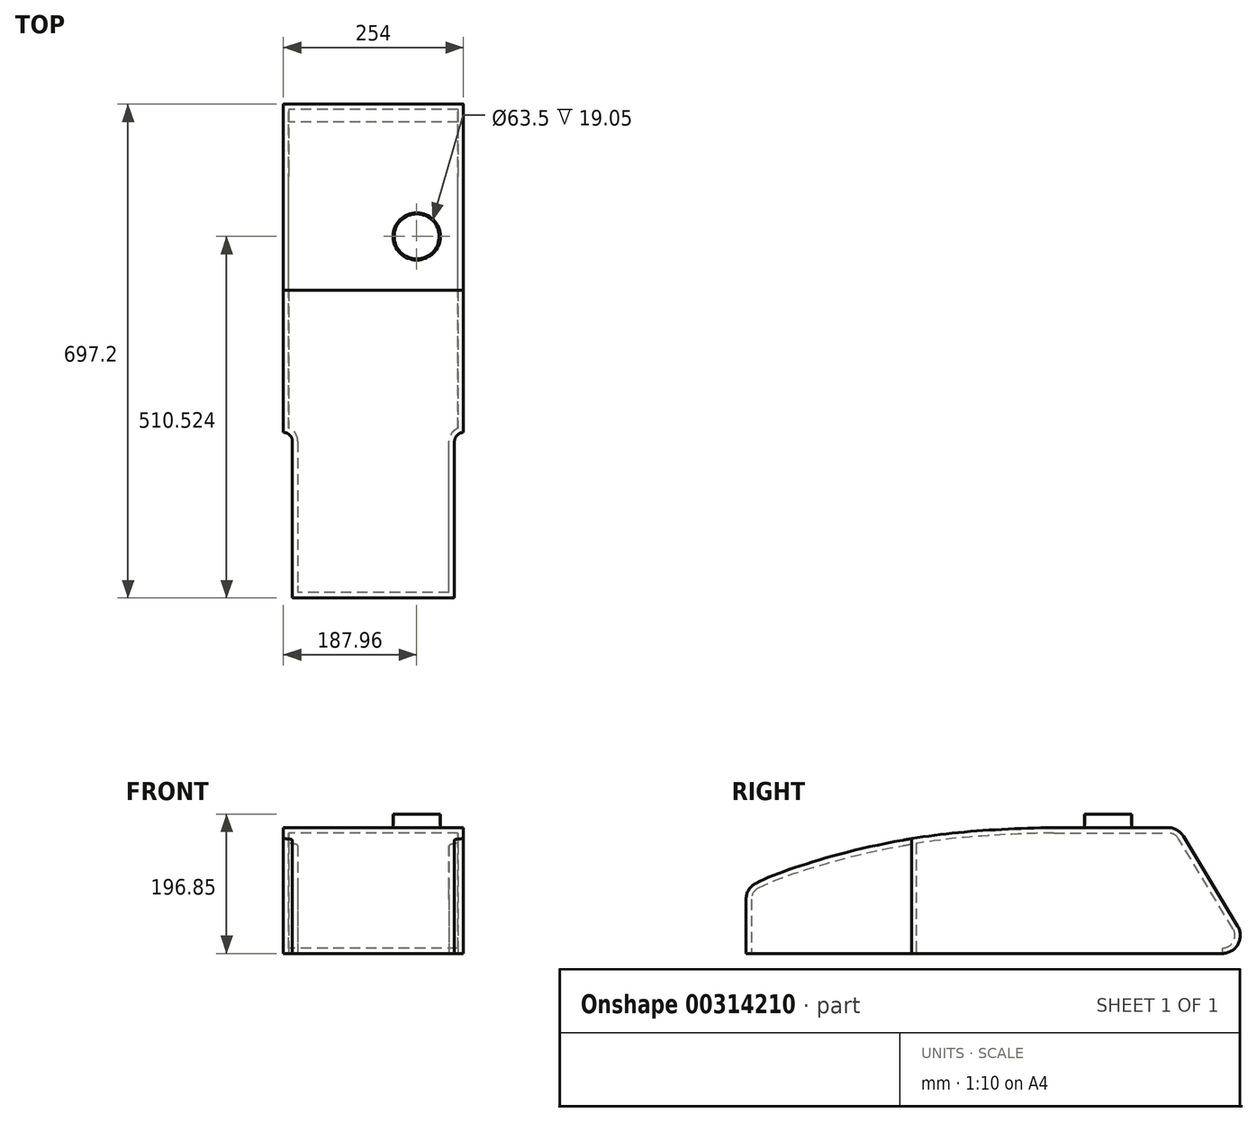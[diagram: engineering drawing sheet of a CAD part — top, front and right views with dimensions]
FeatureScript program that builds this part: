
annotation { "Feature Type Name" : "Feature", "Feature Type Description" : "" }
export const myFeature = defineFeature(function(context is Context, id is Id, definition is map)
    precondition{}
    {
        {
            var Q0;
            Q0=qCreatedBy(makeId("Right.planeOp"),FACE);
            var sketch = newSketch(context, id + "F0", { "sketchPlane" : qUnion([Q0])});
            skLineSegment(sketch, "E0", {"start": v(0, 0) * mm, "end": v(671.8, 0) * mm});
            skLineSegment(sketch, "E1", {"start": v(693.55, 38.52) * mm, "end": v(616.94, 165.52) * mm});
            skLineSegment(sketch, "E2", {"start": v(434.32, 177.8) * mm, "end": v(595.2, 177.8) * mm});
            skLineSegment(sketch, "E3", {"start": v(609.53, 177.8) * mm, "end": v(609.53, 0) * mm, "construction": true});
            skFitSpline(sketch, "E4", {"points": [v(609.53, 177.8) * mm, v(271.41, 167.5) * mm, v(75.93, 123.59) * mm, v(0, 91) * mm, v(-33.15, 62.68) * mm], "startDerivative": vector(-932.62, 8.95) * mm, "endDerivative": vector(-216.23, -214.76) * mm});
            skLineSegment(sketch, "E5", {"start": v(0, 76.41) * mm, "end": v(0, 0) * mm});
            skPoint(sketch, "E6.visualSharp", {"position": v(716.79, 0) * mm});
            skArc(sketch, "E6.filletArc", {"start": v(671.8, 0) * mm, "mid": v(693.92, 12.91) * mm, "end": v(693.55, 38.52) * mm});
            skPoint(sketch, "E7.newPointA", {"position": v(694.44, 177.8) * mm});
            skPoint(sketch, "E7.newPointB", {"position": v(585.59, 217.5) * mm});
            skArc(sketch, "E7.filletArc", {"start": v(616.94, 165.52) * mm, "mid": v(607.68, 174.52) * mm, "end": v(595.2, 177.8) * mm});
            skArc(sketch, "E8.filletArc", {"start": v(13.66, 98.93) * mm, "mid": v(3.68, 89.58) * mm, "end": v(0, 76.41) * mm});
            skPoint(sketch, "E9.orphan", {"position": v(-16.76, 177.8) * mm});
            skSolve(sketch);
        }
        {
            var Q0;
            Q0=makeQuery(id+"F0.imprint","IMPRINT",FACE,{"disambiguationData":[TD([[makeQuery(id+"F0.imprint","IMPRINT",EDGE,{"derivedFrom":sQuery(id+"F0.wireOp",EDGE,"E0")}),1.0]])]});
            extrude(context, id + "F1", {"entities" : qUnion([Q0]), "endBound" : BoundingType.SYMMETRIC, "depth" : 254 * mm});
        }
        {
            var Q0;
            Q0=qCreatedBy(makeId("Top.planeOp"),FACE);
            var sketch = newSketch(context, id + "F2", { "sketchPlane" : qUnion([Q0])});
            skLineSegment(sketch, "E10", {"start": v(0, 0) * mm, "end": v(0, 736.6) * mm, "construction": true});
            skLineSegment(sketch, "E11", {"start": v(0, 0) * mm, "end": v(-114.3, 0) * mm});
            skLineSegment(sketch, "E12", {"start": v(0, 0) * mm, "end": v(114.3, 0) * mm});
            skPoint(sketch, "E13", {"position": v(-114.3, 0) * mm});
            skPoint(sketch, "E14.visualSharp", {"position": v(-114.3, 233.68) * mm});
            skPoint(sketch, "E15.visualSharp", {"position": v(114.3, 233.68) * mm});
            skLineSegment(sketch, "E16", {"start": v(-114.3, 220.98) * mm, "end": v(-114.3, 0) * mm});
            skLineSegment(sketch, "E17", {"start": v(-127, 233.68) * mm, "end": v(-127, 233.68) * mm});
            skLineSegment(sketch, "E18", {"start": v(-114.3, 0) * mm, "end": v(-127, 0) * mm});
            skLineSegment(sketch, "E19", {"start": v(-127, 0) * mm, "end": v(-127, 233.68) * mm});
            skLineSegment(sketch, "E20", {"start": v(114.3, 0) * mm, "end": v(114.3, 220.98) * mm});
            skLineSegment(sketch, "E21", {"start": v(127, 233.68) * mm, "end": v(127, 0) * mm});
            skLineSegment(sketch, "E22", {"start": v(127, 0) * mm, "end": v(114.3, 0) * mm});
            skArc(sketch, "E23.filletArc", {"start": v(-114.3, 220.98) * mm, "mid": v(-118.02, 229.96) * mm, "end": v(-127, 233.68) * mm});
            skLineSegment(sketch, "E24", {"start": v(127, 233.68) * mm, "end": v(127, 233.68) * mm});
            skArc(sketch, "E25.filletArc", {"start": v(127, 233.68) * mm, "mid": v(118.02, 229.96) * mm, "end": v(114.3, 220.98) * mm});
            skSolve(sketch);
        }
        {
            var Q0;
            Q0=makeQuery(id+"F2.imprint","IMPRINT",FACE,{"disambiguationData":[TD([[makeQuery(id+"F2.imprint","IMPRINT",EDGE,{"derivedFrom":sQuery(id+"F2.wireOp",EDGE,"E16")}),-1.0]])]});
            var Q1;
            Q1=makeQuery(id+"F2.imprint","IMPRINT",FACE,{"disambiguationData":[TD([[makeQuery(id+"F2.imprint","IMPRINT",EDGE,{"derivedFrom":sQuery(id+"F2.wireOp",EDGE,"E20")}),-1.0]])]});
            extrude(context, id + "F3", {"entities" : qUnion([Q0, Q1]), "operationType" : NewBodyOperationType.REMOVE, "depth" : 177.8 * mm});
        }
        {
            var Q0;
            Q0=makeQuery(id+"F1.opExtrude","SWEPT_FACE",FACE,{"disambiguationData":[OSD([sQuery(id+"F0.wireOp",EDGE,"E2")])]});
            var sketch = newSketch(context, id + "F4", { "sketchPlane" : qUnion([Q0])});
            skCircle(sketch, "E26", {"center": v(60.96, 510.52) * mm, "radius": 31.75 * mm});
            skLineSegment(sketch, "E27", {"start": v(0, 434.32) * mm, "end": v(0, 638.93) * mm, "construction": true});
            skCircle(sketch, "E28.0", {"center": v(60.96, 510.52) * mm, "radius": 33.34 * mm});
            skSolve(sketch);
        }
        {
            var Q0;
            Q0=makeQuery(id+"F4.imprint","IMPRINT",FACE,{"disambiguationData":[TD([[makeQuery(id+"F4.imprint","IMPRINT",EDGE,{"derivedFrom":sQuery(id+"F4.wireOp",EDGE,"E26")}),-1.0]])]});
            extrude(context, id + "F5", {"entities" : qUnion([Q0]), "operationType" : NewBodyOperationType.ADD, "depth" : 19.05 * mm});
        }
        {
            var Q0;
            Q0=makeQuery(id+"F1.opExtrude","SWEPT_FACE",FACE,{"disambiguationData":[OSD([sQuery(id+"F0.wireOp",EDGE,"E0")])]});
            shell(context, id + "F6", {"entities" : qUnion([Q0]), "thickness" : 7.62 * mm});
        }
    });
